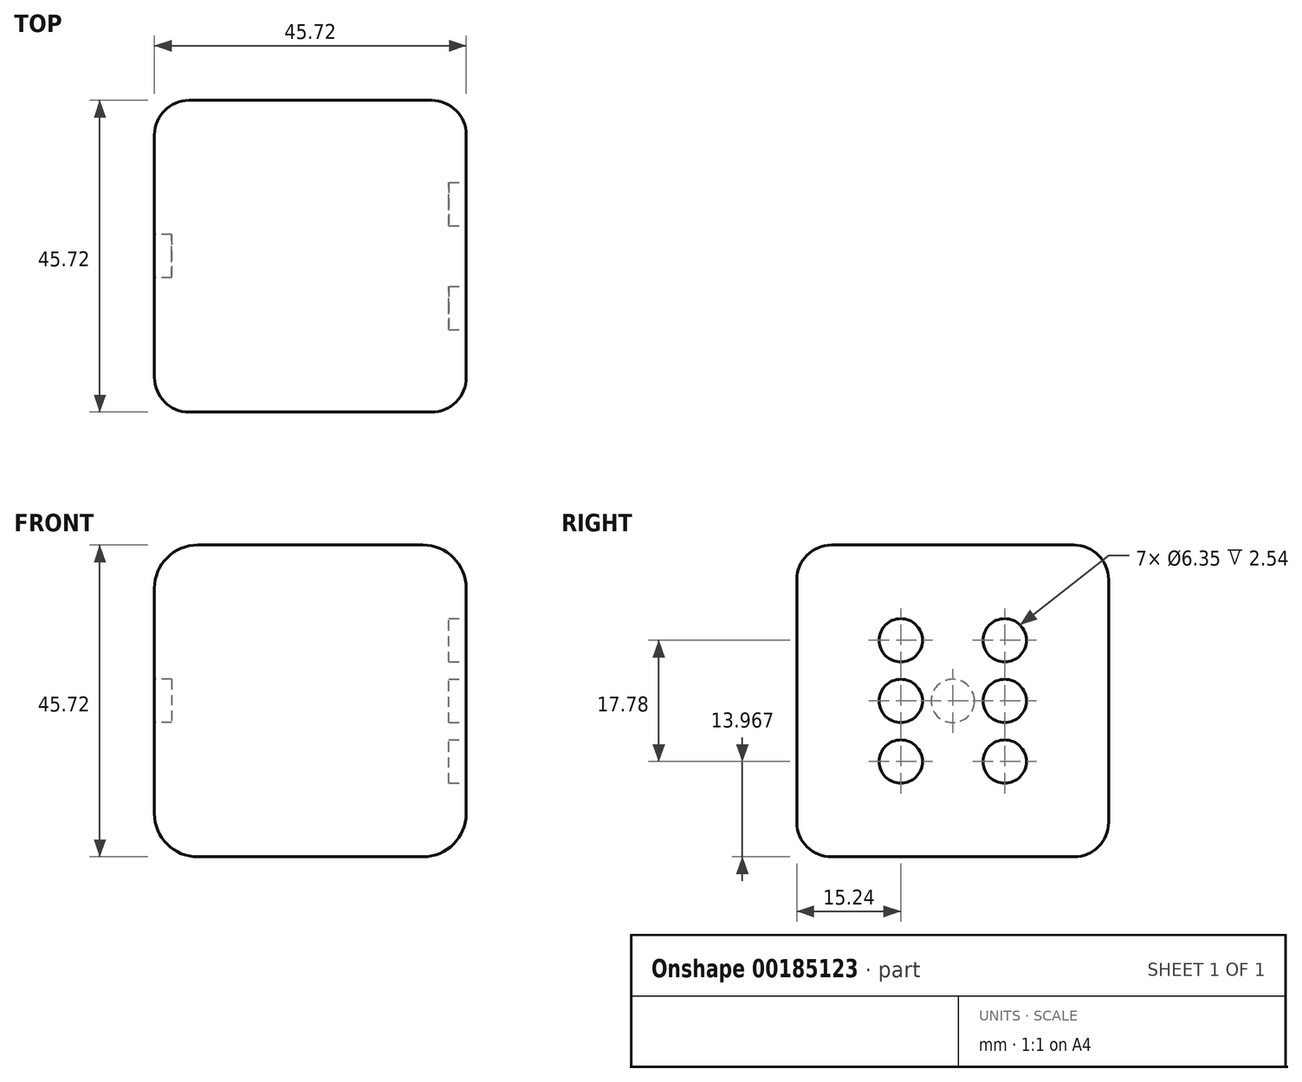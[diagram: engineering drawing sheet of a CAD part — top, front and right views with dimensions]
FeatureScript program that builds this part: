
annotation { "Feature Type Name" : "Feature", "Feature Type Description" : "" }
export const myFeature = defineFeature(function(context is Context, id is Id, definition is map)
    precondition{}
    {
        {
            var Q0;
            Q0=qCreatedBy(makeId("Front.planeOp"),FACE);
            var sketch = newSketch(context, id + "F0", { "sketchPlane" : qUnion([Q0])});
            skLineSegment(sketch, "E0.bottom", {"start": v(-12.38, 16.14) * mm, "end": v(20.64, 16.14) * mm});
            skLineSegment(sketch, "E0.top", {"start": v(-12.38, -29.58) * mm, "end": v(20.64, -29.58) * mm});
            skLineSegment(sketch, "E0.left", {"start": v(-18.73, 9.79) * mm, "end": v(-18.73, -23.23) * mm});
            skLineSegment(sketch, "E0.right", {"start": v(26.99, 9.79) * mm, "end": v(26.99, -23.23) * mm});
            skPoint(sketch, "E1.visualSharp", {"position": v(-18.73, 16.14) * mm});
            skArc(sketch, "E1.filletArc", {"start": v(-12.38, 16.14) * mm, "mid": v(-16.87, 14.28) * mm, "end": v(-18.73, 9.79) * mm});
            skPoint(sketch, "E2.visualSharp", {"position": v(26.99, 16.14) * mm});
            skArc(sketch, "E2.filletArc", {"start": v(26.99, 9.79) * mm, "mid": v(25.13, 14.28) * mm, "end": v(20.64, 16.14) * mm});
            skPoint(sketch, "E3.visualSharp", {"position": v(26.99, -29.58) * mm});
            skArc(sketch, "E3.filletArc", {"start": v(20.64, -29.58) * mm, "mid": v(25.13, -27.72) * mm, "end": v(26.99, -23.23) * mm});
            skPoint(sketch, "E4.visualSharp", {"position": v(-18.73, -29.58) * mm});
            skArc(sketch, "E4.filletArc", {"start": v(-18.73, -23.23) * mm, "mid": v(-16.87, -27.72) * mm, "end": v(-12.38, -29.58) * mm});
            skSolve(sketch);
        }
        {
            var Q0;
            Q0=makeQuery(id+"F0.imprint","IMPRINT",FACE,{"disambiguationData":[TD([[makeQuery(id+"F0.imprint","IMPRINT",EDGE,{"derivedFrom":sQuery(id+"F0.wireOp",EDGE,"E0.bottom")}),-1.0]])]});
            extrude(context, id + "F1", {"entities" : qUnion([Q0]), "endBound" : BoundingType.SYMMETRIC, "depth" : 45.72 * mm});
        }
        {
            var Q0;
            Q0=makeQuery(id+"F1.opExtrude","CAP_EDGE",EDGE,{"disambiguationData":[OSD([sQuery(id+"F0.wireOp",EDGE,"E0.bottom")])],"isStart":false});
            var Q1;
            Q1=makeQuery(id+"F1.opExtrude","CAP_EDGE",EDGE,{"disambiguationData":[OSD([sQuery(id+"F0.wireOp",EDGE,"E0.bottom")])],"isStart":true});
            fillet(context, id + "F2", {"entities" : qUnion([Q0, Q1]), "radius" : 5.08 * mm, "tangentPropagation" : true, "allowEdgeOverflow" : false});
        }
        {
            var Q0;
            Q0=makeQuery(id+"F1.opExtrude","SWEPT_FACE",FACE,{"disambiguationData":[OSD([sQuery(id+"F0.wireOp",EDGE,"E0.left")])]});
            var sketch = newSketch(context, id + "F3", { "sketchPlane" : qUnion([Q0])});
            skCircle(sketch, "E5", {"center": v(0, -6.72) * mm, "radius": 3.18 * mm});
            skPoint(sketch, "E5.centerSnap0", {"position": v(17.78, -6.72) * mm});
            skPoint(sketch, "E5.centerSnap1", {"position": v(0, -23.23) * mm});
            skSolve(sketch);
        }
        {
            var Q0;
            Q0=makeQuery(id+"F3.imprint","IMPRINT",FACE,{"disambiguationData":[TD([[makeQuery(id+"F3.imprint","IMPRINT",EDGE,{"derivedFrom":sQuery(id+"F3.wireOp",EDGE,"E5")}),1.0]])]});
            extrude(context, id + "F4", {"entities" : qUnion([Q0]), "operationType" : NewBodyOperationType.REMOVE, "oppositeDirection" : true, "depth" : 2.54 * mm});
        }
        {
            var Q0;
            Q0=makeQuery(id+"F1.opExtrude","SWEPT_FACE",FACE,{"disambiguationData":[OSD([sQuery(id+"F0.wireOp",EDGE,"E0.right")])]});
            var sketch = newSketch(context, id + "F5", { "sketchPlane" : qUnion([Q0])});
            skCircle(sketch, "E6", {"center": v(-7.62, 2.17) * mm, "radius": 3.18 * mm});
            skCircle(sketch, "E7", {"center": v(7.62, 2.17) * mm, "radius": 3.18 * mm});
            skCircle(sketch, "E8", {"center": v(7.62, -15.61) * mm, "radius": 3.18 * mm});
            skCircle(sketch, "E9", {"center": v(7.62, -6.72) * mm, "radius": 3.18 * mm});
            skCircle(sketch, "E10", {"center": v(-7.62, -6.72) * mm, "radius": 3.18 * mm});
            skCircle(sketch, "E11", {"center": v(-7.62, -15.61) * mm, "radius": 3.18 * mm});
            skLineSegment(sketch, "E12.0", {"start": v(-7.62, 9.79) * mm, "end": v(-7.62, -23.23) * mm, "construction": true});
            skLineSegment(sketch, "E13.MirrorCS", {"start": v(7.62, 9.79) * mm, "end": v(7.62, -23.23) * mm, "construction": true});
            skLineSegment(sketch, "E14", {"start": v(17.78, -6.72) * mm, "end": v(-17.78, -6.72) * mm, "construction": true});
            skLineSegment(sketch, "E15.0", {"start": v(-17.78, 2.17) * mm, "end": v(17.78, 2.17) * mm, "construction": true});
            skLineSegment(sketch, "E16.MirrorCS", {"start": v(-17.78, -15.61) * mm, "end": v(17.78, -15.61) * mm, "construction": true});
            skSolve(sketch);
        }
        {
            var Q0;
            Q0=makeQuery(id+"F5.imprint","IMPRINT",FACE,{"disambiguationData":[TD([[makeQuery(id+"F5.imprint","IMPRINT",EDGE,{"derivedFrom":sQuery(id+"F5.wireOp",EDGE,"E6")}),1.0]])]});
            var Q1;
            Q1=makeQuery(id+"F5.imprint","IMPRINT",FACE,{"disambiguationData":[TD([[makeQuery(id+"F5.imprint","IMPRINT",EDGE,{"derivedFrom":sQuery(id+"F5.wireOp",EDGE,"E7")}),1.0]])]});
            var Q2;
            Q2=makeQuery(id+"F5.imprint","IMPRINT",FACE,{"disambiguationData":[TD([[makeQuery(id+"F5.imprint","IMPRINT",EDGE,{"derivedFrom":sQuery(id+"F5.wireOp",EDGE,"E9")}),1.0]])]});
            var Q3;
            Q3=makeQuery(id+"F5.imprint","IMPRINT",FACE,{"disambiguationData":[TD([[makeQuery(id+"F5.imprint","IMPRINT",EDGE,{"derivedFrom":sQuery(id+"F5.wireOp",EDGE,"E10")}),1.0]])]});
            var Q4;
            Q4=makeQuery(id+"F5.imprint","IMPRINT",FACE,{"disambiguationData":[TD([[makeQuery(id+"F5.imprint","IMPRINT",EDGE,{"derivedFrom":sQuery(id+"F5.wireOp",EDGE,"E11")}),1.0]])]});
            var Q5;
            Q5=makeQuery(id+"F5.imprint","IMPRINT",FACE,{"disambiguationData":[TD([[makeQuery(id+"F5.imprint","IMPRINT",EDGE,{"derivedFrom":sQuery(id+"F5.wireOp",EDGE,"E8")}),1.0]])]});
            extrude(context, id + "F6", {"entities" : qUnion([Q0, Q1, Q2, Q3, Q4, Q5]), "operationType" : NewBodyOperationType.REMOVE, "oppositeDirection" : true, "depth" : 2.54 * mm});
        }
    });
